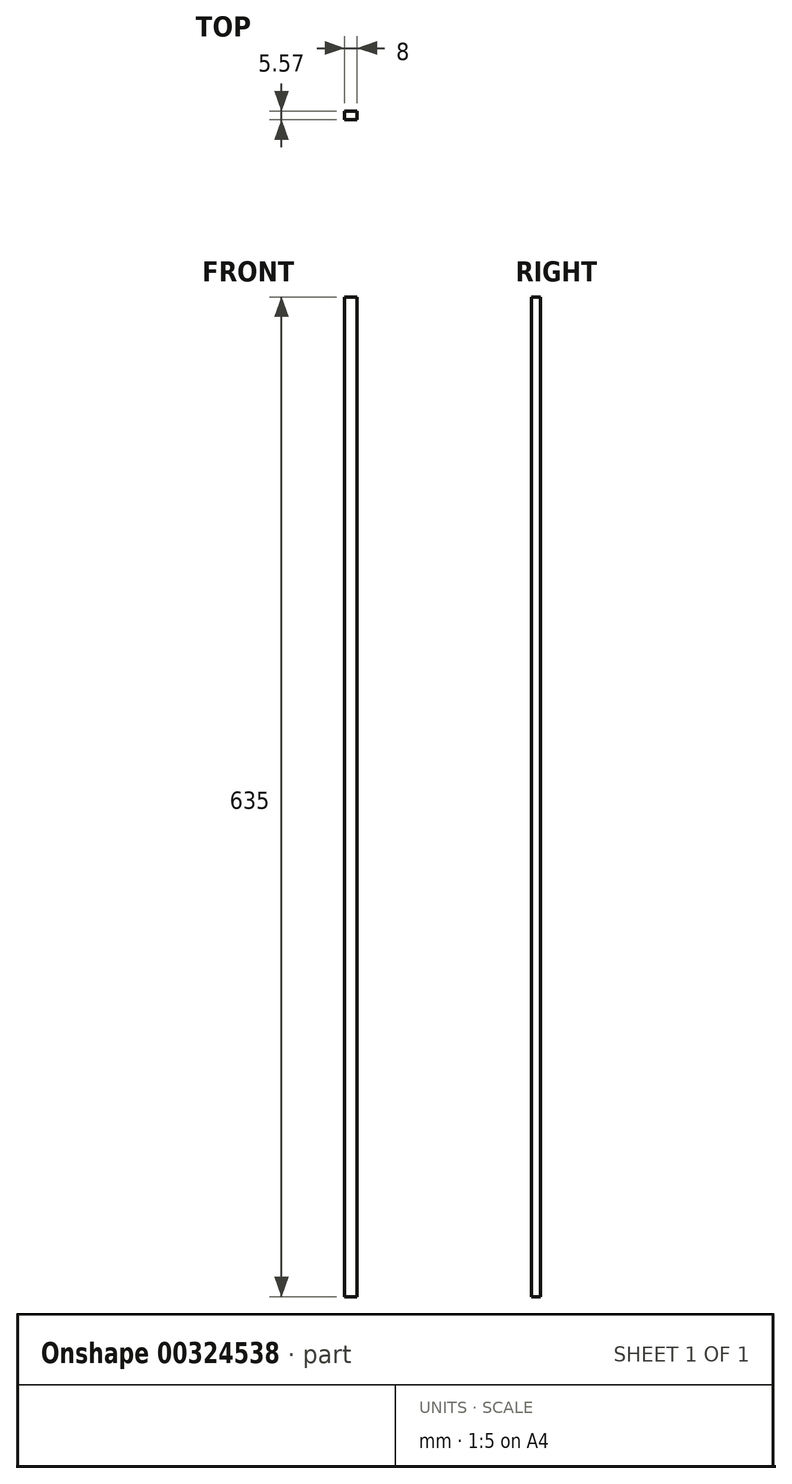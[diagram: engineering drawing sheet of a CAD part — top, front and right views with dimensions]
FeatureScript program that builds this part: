
annotation { "Feature Type Name" : "Feature", "Feature Type Description" : "" }
export const myFeature = defineFeature(function(context is Context, id is Id, definition is map)
    precondition{}
    {
        {
            var Q0;
            Q0=qCreatedBy(makeId("Top.planeOp"),FACE);
            var sketch = newSketch(context, id + "F0", { "sketchPlane" : qUnion([Q0])});
            skLineSegment(sketch, "E0.bottom", {"start": v(0, 0) * mm, "end": v(8, 0) * mm});
            skLineSegment(sketch, "E0.top", {"start": v(0, 5.57) * mm, "end": v(8, 5.57) * mm});
            skLineSegment(sketch, "E0.left", {"start": v(0, 0) * mm, "end": v(0, 5.57) * mm});
            skLineSegment(sketch, "E0.right", {"start": v(8, 0) * mm, "end": v(8, 5.57) * mm});
            skSolve(sketch);
        }
        {
            var Q0;
            Q0 = qSketchRegion(id + "F0", true);
            extrude(context, id + "F1", {"entities" : qUnion([Q0]), "depth" : 635 * mm});
        }
    });
